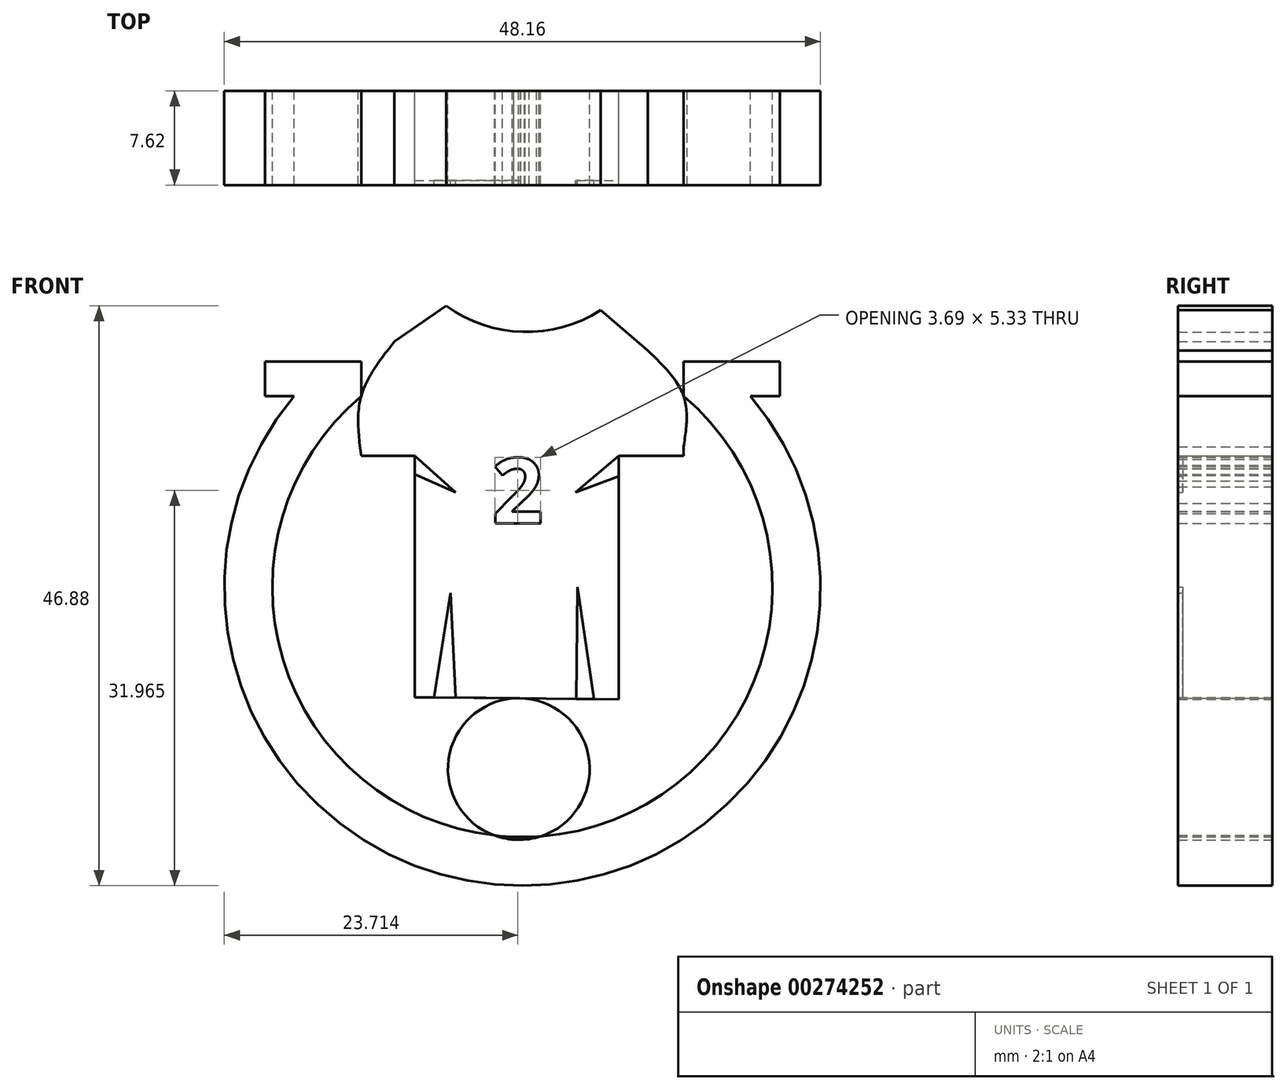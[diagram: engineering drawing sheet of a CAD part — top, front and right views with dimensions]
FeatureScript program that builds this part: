
annotation { "Feature Type Name" : "Feature", "Feature Type Description" : "" }
export const myFeature = defineFeature(function(context is Context, id is Id, definition is map)
    precondition{}
    {
        {
            var Q0;
            Q0=qCreatedBy(makeId("Front.planeOp"),FACE);
            var sketch = newSketch(context, id + "F0", { "sketchPlane" : qUnion([Q0])});
            skArc(sketch, "E0", {"start": v(-64.97, 48.24) * mm, "mid": v(-46.54, 8.66) * mm, "end": v(-28.1, 48.24) * mm});
            skLineSegment(sketch, "E1", {"start": v(-64.97, 48.24) * mm, "end": v(-59.56, 48.24) * mm});
            skLineSegment(sketch, "E2", {"start": v(-28.1, 48.24) * mm, "end": v(-33.52, 48.24) * mm});
            skArc(sketch, "E3", {"start": v(-59.56, 48.24) * mm, "mid": v(-46.54, 12.6) * mm, "end": v(-33.52, 48.24) * mm});
            skLineSegment(sketch, "E4.bottom", {"start": v(-59.56, 48.24) * mm, "end": v(-67.34, 48.24) * mm});
            skLineSegment(sketch, "E4.top", {"start": v(-59.56, 51.02) * mm, "end": v(-67.34, 51.02) * mm});
            skLineSegment(sketch, "E4.left", {"start": v(-59.56, 48.24) * mm, "end": v(-59.56, 51.02) * mm});
            skLineSegment(sketch, "E4.right", {"start": v(-67.34, 48.24) * mm, "end": v(-67.34, 51.02) * mm});
            skLineSegment(sketch, "E5.bottom", {"start": v(-33.52, 48.24) * mm, "end": v(-25.73, 48.24) * mm});
            skLineSegment(sketch, "E5.top", {"start": v(-33.52, 51.02) * mm, "end": v(-25.73, 51.02) * mm});
            skLineSegment(sketch, "E5.left", {"start": v(-33.52, 48.24) * mm, "end": v(-33.52, 51.02) * mm});
            skLineSegment(sketch, "E5.right", {"start": v(-25.73, 48.24) * mm, "end": v(-25.73, 51.02) * mm});
            skLineSegment(sketch, "E6", {"start": v(-56.87, 52.64) * mm, "end": v(-52.7, 55.54) * mm});
            skFitSpline(sketch, "E7", {"points": [v(-56.87, 52.64) * mm, v(-59.56, 48.24) * mm, v(-59.56, 43.4) * mm], "startDerivative": vector(-6.63, -8.37) * mm, "endDerivative": vector(1.3, -10.12) * mm});
            skLineSegment(sketch, "E8", {"start": v(-59.56, 43.4) * mm, "end": v(-55.24, 43.4) * mm});
            skLineSegment(sketch, "E9", {"start": v(-36.4, 51.91) * mm, "end": v(-40.2, 55.18) * mm});
            skArc(sketch, "E10", {"start": v(-52.7, 55.54) * mm, "mid": v(-46.51, 53.43) * mm, "end": v(-40.2, 55.18) * mm});
            skFitSpline(sketch, "E11", {"points": [v(-36.4, 51.91) * mm, v(-33.52, 48.24) * mm, v(-33.52, 44.13) * mm], "startDerivative": vector(7.03, -6.77) * mm, "endDerivative": vector(-1.35, -8.83) * mm});
            skLineSegment(sketch, "E12", {"start": v(-33.52, 43.4) * mm, "end": v(-38.76, 43.4) * mm});
            skLineSegment(sketch, "E13", {"start": v(-55.24, 43.4) * mm, "end": v(-55.24, 23.89) * mm});
            skLineSegment(sketch, "E14", {"start": v(-38.76, 43.4) * mm, "end": v(-38.76, 23.72) * mm});
            skLineSegment(sketch, "E15", {"start": v(-38.76, 23.72) * mm, "end": v(-55.24, 23.89) * mm});
            skText(sketch, "E16", { "text": "2", "fontName": "OpenSans-Bold.ttf"});
            skPoint(sketch, "E17.endSnap0", {"position": v(-55.24, 33.64) * mm});
            skLineSegment(sketch, "E18", {"start": v(-51.94, 23.89) * mm, "end": v(-40.75, 23.74) * mm});
            skLineSegment(sketch, "E19", {"start": v(-40.75, 23.74) * mm, "end": v(-42.08, 32.8) * mm});
            skLineSegment(sketch, "E20", {"start": v(-42.08, 32.8) * mm, "end": v(-42.17, 23.76) * mm});
            skLineSegment(sketch, "E21", {"start": v(-53.66, 23.87) * mm, "end": v(-52.34, 32.33) * mm});
            skLineSegment(sketch, "E22", {"start": v(-52.34, 32.33) * mm, "end": v(-51.94, 23.89) * mm});
            skLineSegment(sketch, "E23", {"start": v(-55.24, 43.4) * mm, "end": v(-51.94, 40.44) * mm});
            skLineSegment(sketch, "E24", {"start": v(-51.94, 40.44) * mm, "end": v(-55.24, 41.92) * mm});
            skPoint(sketch, "E24.endSnap0", {"position": v(-53.6, 41.92) * mm});
            skLineSegment(sketch, "E25", {"start": v(-38.76, 43.4) * mm, "end": v(-42.24, 40.44) * mm});
            skLineSegment(sketch, "E26", {"start": v(-42.24, 40.44) * mm, "end": v(-38.76, 41.76) * mm});
            skPoint(sketch, "E27.0.internal.snap0", {"position": v(-59.56, 49.63) * mm});
            skCircle(sketch, "E28", {"center": v(-46.83, 18.1) * mm, "radius": 5.73 * mm});
            skArc(sketch, "E29", {"start": v(-43.57, 22.8) * mm, "mid": v(-44.96, 18.09) * mm, "end": v(-43.63, 13.35) * mm});
            skArc(sketch, "E30", {"start": v(-49.97, 13.31) * mm, "mid": v(-48.17, 18.14) * mm, "end": v(-49.63, 23.09) * mm});
            skLineSegment(sketch, "E31", {"start": v(-49.77, 22.18) * mm, "end": v(-48.87, 22.76) * mm});
            skLineSegment(sketch, "E32", {"start": v(-49.3, 21.65) * mm, "end": v(-48.5, 22.18) * mm});
            skLineSegment(sketch, "E33", {"start": v(-49.13, 20.96) * mm, "end": v(-48.07, 21.43) * mm});
            skLineSegment(sketch, "E34", {"start": v(-48.97, 20.32) * mm, "end": v(-47.86, 20.66) * mm});
            skLineSegment(sketch, "E35", {"start": v(-48.87, 19.77) * mm, "end": v(-47.78, 19.93) * mm});
            skLineSegment(sketch, "E36", {"start": v(-48.87, 19.2) * mm, "end": v(-47.74, 19.2) * mm});
            skLineSegment(sketch, "E37", {"start": v(-48.85, 18.62) * mm, "end": v(-47.73, 18.52) * mm});
            skLineSegment(sketch, "E38", {"start": v(-48.9, 18.07) * mm, "end": v(-47.82, 17.83) * mm});
            skLineSegment(sketch, "E39", {"start": v(-48.92, 17.57) * mm, "end": v(-47.76, 17.23) * mm});
            skLineSegment(sketch, "E40", {"start": v(-49, 17.06) * mm, "end": v(-47.9, 16.62) * mm});
            skLineSegment(sketch, "E41", {"start": v(-49.07, 16.36) * mm, "end": v(-48.13, 15.89) * mm});
            skLineSegment(sketch, "E42", {"start": v(-49.23, 15.84) * mm, "end": v(-48.34, 15.32) * mm});
            skLineSegment(sketch, "E43", {"start": v(-49.43, 15.28) * mm, "end": v(-48.48, 14.7) * mm});
            skLineSegment(sketch, "E44", {"start": v(-49.73, 14.76) * mm, "end": v(-48.85, 14.19) * mm});
            skLineSegment(sketch, "E45", {"start": v(-49.99, 14.39) * mm, "end": v(-49.15, 13.75) * mm});
            skLineSegment(sketch, "E46", {"start": v(-50.19, 13.99) * mm, "end": v(-49.38, 13.32) * mm});
            skLineSegment(sketch, "E47", {"start": v(-44.35, 22.87) * mm, "end": v(-43.18, 22.04) * mm});
            skLineSegment(sketch, "E48", {"start": v(-44.59, 22.43) * mm, "end": v(-43.48, 21.57) * mm});
            skLineSegment(sketch, "E49", {"start": v(-44.8, 21.68) * mm, "end": v(-43.71, 21.13) * mm});
            skLineSegment(sketch, "E50", {"start": v(-45.04, 20.96) * mm, "end": v(-43.78, 20.49) * mm});
            skLineSegment(sketch, "E51", {"start": v(-45.25, 20.32) * mm, "end": v(-43.95, 19.87) * mm});
            skLineSegment(sketch, "E52", {"start": v(-45.36, 19.42) * mm, "end": v(-44.12, 19.14) * mm});
            skLineSegment(sketch, "E53", {"start": v(-45.4, 18.63) * mm, "end": v(-44.23, 18.42) * mm});
            skLineSegment(sketch, "E54", {"start": v(-45.68, 18.03) * mm, "end": v(-44.3, 17.76) * mm});
            skLineSegment(sketch, "E55", {"start": v(-45.61, 17.16) * mm, "end": v(-44.18, 17.16) * mm});
            skLineSegment(sketch, "E56", {"start": v(-45.38, 16.29) * mm, "end": v(-44.06, 16.46) * mm});
            skLineSegment(sketch, "E57", {"start": v(-45.19, 15.46) * mm, "end": v(-44, 15.84) * mm});
            skLineSegment(sketch, "E58", {"start": v(-44.97, 14.69) * mm, "end": v(-43.7, 15.24) * mm});
            skLineSegment(sketch, "E59", {"start": v(-44.57, 14.1) * mm, "end": v(-43.37, 14.69) * mm});
            skLineSegment(sketch, "E60", {"start": v(-44.2, 13.52) * mm, "end": v(-43.27, 14.16) * mm});
            skLineSegment(sketch, "E61", {"start": v(-33.52, 44.13) * mm, "end": v(-33.52, 43.4) * mm});
            const initialGuessF0  = {"E16": [-0.04903, 0.03796, 1, 0, 0.0053]};
            skSetInitialGuess(sketch, initialGuessF0);
            skSolve(sketch);
        }
        {
            var Q0;
            {var subQ1=sQuery(id+"F0.wireOp",EDGE,"E0");Q0=makeQuery(id+"F0.imprint","IMPRINT",FACE,{"disambiguationData":[TD([[makeQuery(id+"F0.imprint","IMPRINT",EDGE,{"derivedFrom":subQ1}),1.0]])]});}
            var Q1;
            Q1=makeQuery(id+"F0.imprint","IMPRINT",FACE,{"disambiguationData":[TD([[makeQuery(id+"F0.imprint","IMPRINT",EDGE,{"derivedFrom":sQuery(id+"F0.wireOp",EDGE,"E5.top")}),-1.0]])]});
            var Q2;
            Q2=makeQuery(id+"F0.imprint","IMPRINT",FACE,{"disambiguationData":[TD([[makeQuery(id+"F0.imprint","IMPRINT",EDGE,{"derivedFrom":sQuery(id+"F0.wireOp",EDGE,"E4.top")}),1.0]])]});
            var Q3;
            {var subQ13=sQuery(id+"F0.wireOp",EDGE,"E6");Q3=makeQuery(id+"F0.imprint","IMPRINT",FACE,{"disambiguationData":[TD([[makeQuery(id+"F0.imprint","IMPRINT",EDGE,{"derivedFrom":subQ13}),-1.0]])]});}
            var Q4;
            {var subQ0=sQuery(id+"F0.wireOp",EDGE,"E29");var subQ36=makeQuery(id+"F0.imprint","IMPRINT",VERTEX,{"disambiguationData":[OD(0.0)],"derivedFrom":subQ0});Q4=makeQuery(id+"F0.imprint","IMPRINT",FACE,{"disambiguationData":[TD([[makeQuery(id+"F0.imprint","IMPRINT",EDGE,{"disambiguationData":[TD([[subQ36,-1.0]])],"derivedFrom":subQ0}),-1.0]])]});}
            var Q5;
            {var subQ0=sQuery(id+"F0.wireOp",EDGE,"E30");var subQ14=makeQuery(id+"F0.imprint","IMPRINT",VERTEX,{"disambiguationData":[OD(0.0)],"derivedFrom":subQ0});Q5=makeQuery(id+"F0.imprint","IMPRINT",FACE,{"disambiguationData":[TD([[makeQuery(id+"F0.imprint","IMPRINT",EDGE,{"disambiguationData":[TD([[subQ14,-1.0]])],"derivedFrom":subQ0}),1.0]])]});}
            var Q6;
            {var subQ0=sQuery(id+"F0.wireOp",EDGE,"E29");var subQ11=makeQuery(id+"F0.imprint","IMPRINT",VERTEX,{"disambiguationData":[OD(0.0)],"derivedFrom":subQ0});Q6=makeQuery(id+"F0.imprint","IMPRINT",FACE,{"disambiguationData":[TD([[makeQuery(id+"F0.imprint","IMPRINT",EDGE,{"disambiguationData":[TD([[subQ11,-1.0]])],"derivedFrom":subQ0}),1.0]])]});}
            extrude(context, id + "F1", {"entities" : qUnion([Q0, Q1, Q2, Q3, Q4, Q5, Q6]), "depth" : 7.62 * mm});
        }
        {
            var Q0;
            {var subQ6=sQuery(id+"F0.wireOp",EDGE,"E21");Q0=makeQuery(id+"F0.imprint","IMPRINT",FACE,{"disambiguationData":[TD([[makeQuery(id+"F0.imprint","IMPRINT",EDGE,{"derivedFrom":subQ6}),-1.0]])]});}
            var Q1;
            {var subQ0=sQuery(id+"F0.wireOp",EDGE,"E19");Q1=makeQuery(id+"F0.imprint","IMPRINT",FACE,{"disambiguationData":[TD([[makeQuery(id+"F0.imprint","IMPRINT",EDGE,{"derivedFrom":subQ0}),1.0]])]});}
            var Q2;
            {var subQ0=sQuery(id+"F0.wireOp",EDGE,"E23");Q2=makeQuery(id+"F0.imprint","IMPRINT",FACE,{"disambiguationData":[TD([[makeQuery(id+"F0.imprint","IMPRINT",EDGE,{"derivedFrom":subQ0}),-1.0]])]});}
            var Q3;
            {var subQ0=sQuery(id+"F0.wireOp",EDGE,"E25");Q3=makeQuery(id+"F0.imprint","IMPRINT",FACE,{"disambiguationData":[TD([[makeQuery(id+"F0.imprint","IMPRINT",EDGE,{"derivedFrom":subQ0}),1.0]])]});}
            extrude(context, id + "F2", {"entities" : qUnion([Q0, Q1, Q2, Q3]), "operationType" : NewBodyOperationType.ADD, "depth" : 7.24 * mm});
        }
        {
            var Q0;
            Q0=sQuery(id+"F0.wireOp",EDGE,"E31");
            var Q1;
            Q1=sQuery(id+"F0.wireOp",EDGE,"E32");
            var Q2;
            Q2=sQuery(id+"F0.wireOp",EDGE,"E33");
            var Q3;
            Q3=sQuery(id+"F0.wireOp",EDGE,"E34");
            var Q4;
            Q4=sQuery(id+"F0.wireOp",EDGE,"E35");
            var Q5;
            Q5=sQuery(id+"F0.wireOp",EDGE,"E36");
            var Q6;
            Q6=sQuery(id+"F0.wireOp",EDGE,"E37");
            var Q7;
            Q7=sQuery(id+"F0.wireOp",EDGE,"E38");
            extrude(context, id + "F3", {"bodyType" : ToolBodyType.SURFACE, "surfaceEntities" : qUnion([Q0, Q1, Q2, Q3, Q4, Q5, Q6, Q7]), "depth" : 8.13 * mm});
        }
        {
            var Q0;
            Q0=sQuery(id+"F0.wireOp",EDGE,"E36");
            var Q1;
            Q1=sQuery(id+"F0.wireOp",EDGE,"E37");
            var Q2;
            Q2=sQuery(id+"F0.wireOp",EDGE,"E38");
            var Q3;
            Q3=sQuery(id+"F0.wireOp",EDGE,"E39");
            var Q4;
            Q4=sQuery(id+"F0.wireOp",EDGE,"E40");
            var Q5;
            Q5=sQuery(id+"F0.wireOp",EDGE,"E41");
            var Q6;
            Q6=sQuery(id+"F0.wireOp",EDGE,"E42");
            var Q7;
            Q7=sQuery(id+"F0.wireOp",EDGE,"E43");
            var Q8;
            Q8=sQuery(id+"F0.wireOp",EDGE,"E44");
            var Q9;
            Q9=sQuery(id+"F0.wireOp",EDGE,"E45");
            var Q10;
            Q10=sQuery(id+"F0.wireOp",EDGE,"E46");
            var Q11;
            Q11=sQuery(id+"F0.wireOp",EDGE,"E47");
            var Q12;
            Q12=sQuery(id+"F0.wireOp",EDGE,"E48");
            var Q13;
            Q13=sQuery(id+"F0.wireOp",EDGE,"E49");
            var Q14;
            Q14=sQuery(id+"F0.wireOp",EDGE,"E50");
            var Q15;
            Q15=sQuery(id+"F0.wireOp",EDGE,"E51");
            var Q16;
            Q16=sQuery(id+"F0.wireOp",EDGE,"E52");
            var Q17;
            Q17=sQuery(id+"F0.wireOp",EDGE,"E53");
            var Q18;
            Q18=sQuery(id+"F0.wireOp",EDGE,"E54");
            var Q19;
            Q19=sQuery(id+"F0.wireOp",EDGE,"E55");
            var Q20;
            Q20=sQuery(id+"F0.wireOp",EDGE,"E56");
            var Q21;
            Q21=sQuery(id+"F0.wireOp",EDGE,"E57");
            var Q22;
            Q22=sQuery(id+"F0.wireOp",EDGE,"E58");
            var Q23;
            Q23=sQuery(id+"F0.wireOp",EDGE,"E59");
            var Q24;
            Q24=sQuery(id+"F0.wireOp",EDGE,"E60");
            extrude(context, id + "F4", {"bodyType" : ToolBodyType.SURFACE, "surfaceEntities" : qUnion([Q0, Q1, Q2, Q3, Q4, Q5, Q6, Q7, Q8, Q9, Q10, Q11, Q12, Q13, Q14, Q15, Q16, Q17, Q18, Q19, Q20, Q21, Q22, Q23, Q24]), "depth" : 8.13 * mm});
        }
    });
